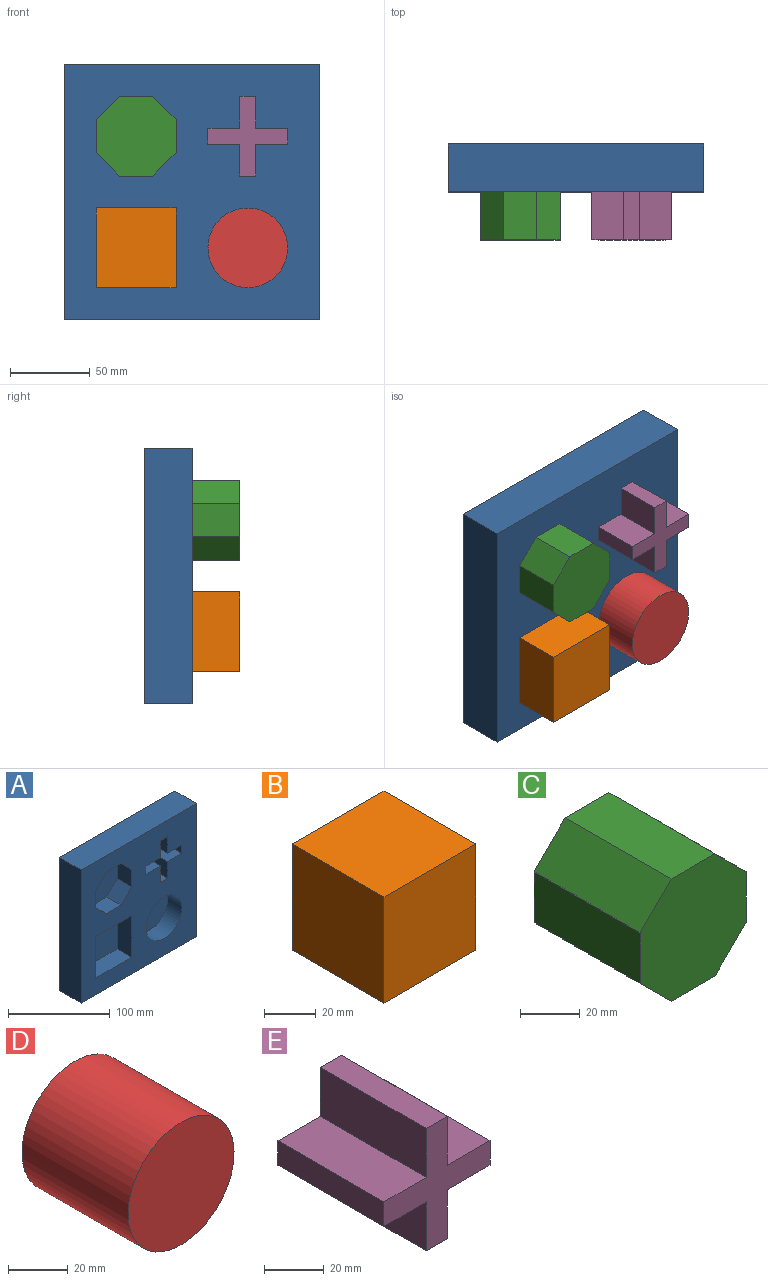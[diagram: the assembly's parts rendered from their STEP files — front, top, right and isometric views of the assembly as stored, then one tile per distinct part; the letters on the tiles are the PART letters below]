
ASSEMBLY  parts=5 mates=4
PART A: 35 faces, bbox 160x30x160 mm
  f0: plane 160x160mm, normal (0,-1,0), area 18165.4mm2, adj f1,f2,f3,f4,f6,f7,f8,f9
  f1: plane 160x30mm, normal (0,0,1), area 4800mm2, adj f0,f2,f4,f5
  f2: plane 160x30mm, normal (-1,0,0), area 4800mm2, adj f0,f1,f3,f5
  f3: plane 160x30mm, normal (0,0,-1), area 4800mm2, adj f0,f2,f4,f5
  f4: plane 160x30mm, normal (1,0,0), area 4800mm2, adj f0,f1,f3,f5
  f5: plane 160x160mm, normal (0,1,0), area 25600mm2, adj f1,f2,f3,f4
  f6: plane 20x14.64mm, normal (-0.71,0,-0.71), area 414.2mm2, adj f0,f7,f13,f14
  f7: plane 20.71x20mm, normal (0,0,-1), area 414.2mm2, adj f0,f6,f8,f14
  f8: plane 20x14.64mm, normal (0.71,0,-0.71), area 414.2mm2, adj f0,f7,f9,f14
  f9: plane 20.71x20mm, normal (1,0,0), area 414.2mm2, adj f0,f8,f10,f14
  f10: plane 20x14.64mm, normal (0.71,0,0.71), area 414.2mm2, adj f0,f9,f11,f14
  f11: plane 20.71x20mm, normal (0,0,1), area 414.2mm2, adj f0,f10,f12,f14
  f12: plane 20x14.64mm, normal (-0.71,0,0.71), area 414.2mm2, adj f0,f11,f13,f14
  f13: plane 20.71x20mm, normal (-1,0,0), area 414.2mm2, adj f0,f6,f12,f14
  f14: plane 50x50mm, normal (0,-1,0), area 2071.1mm2, adj f6,f7,f8,f9,f10,f11,f12,f13
  f15: cylinder r=25mm len=50mm, axis (0,-1,0), area 3141.6mm2, adj f0,f16
  f16: plane 50x50mm, normal (0,-1,0), area 1963.5mm2, adj f15
  f17: plane 50x20mm, normal (0,0,-1), area 1000mm2, adj f0,f18,f20,f21
  f18: plane 50x20mm, normal (1,0,0), area 1000mm2, adj f0,f17,f19,f21
  f19: plane 50x20mm, normal (0,0,1), area 1000mm2, adj f0,f18,f20,f21
  f20: plane 50x20mm, normal (-1,0,0), area 1000mm2, adj f0,f17,f19,f21
  f21: plane 50x50mm, normal (0,-1,0), area 2500mm2, adj f17,f18,f19,f20
  f22: plane 20x10mm, normal (0,0,-1), area 200mm2, adj f0,f23,f33,f34
  f23: plane 20x20mm, normal (1,0,0), area 400mm2, adj f0,f22,f24,f34
  f24: plane 20x20mm, normal (0,0,-1), area 400mm2, adj f0,f23,f25,f34
  f25: plane 20x10mm, normal (1,0,0), area 200mm2, adj f0,f24,f26,f34
  f26: plane 20x20mm, normal (0,0,1), area 400mm2, adj f0,f25,f27,f34
  f27: plane 20x20mm, normal (1,0,0), area 400mm2, adj f0,f26,f28,f34
  f28: plane 20x10mm, normal (0,0,1), area 200mm2, adj f0,f27,f29,f34
  f29: plane 20x20mm, normal (-1,0,0), area 400mm2, adj f0,f28,f30,f34
  f30: plane 20x20mm, normal (0,0,1), area 400mm2, adj f0,f29,f31,f34
  f31: plane 20x10mm, normal (-1,0,0), area 200mm2, adj f0,f30,f32,f34
  f32: plane 20x20mm, normal (0,0,-1), area 400mm2, adj f0,f31,f33,f34
  f33: plane 20x20mm, normal (-1,0,0), area 400mm2, adj f0,f22,f32,f34
  f34: plane 50x50mm, normal (0,-1,0), area 900mm2, adj f22,f23,f24,f25,f26,f27,f28,f29
PART B: 6 faces, bbox 50x50x50 mm
  f0: plane 50x50mm, normal (0,0,1), area 2500mm2, adj f1,f3,f4,f5
  f1: plane 50x50mm, normal (-1,0,0), area 2500mm2, adj f0,f2,f4,f5
  f2: plane 50x50mm, normal (0,0,-1), area 2500mm2, adj f1,f3,f4,f5
  f3: plane 50x50mm, normal (1,0,0), area 2500mm2, adj f0,f2,f4,f5
  f4: plane 50x50mm, normal (0,-1,0), area 2500mm2, adj f0,f1,f2,f3
  f5: plane 50x50mm, normal (0,1,0), area 2500mm2, adj f0,f1,f2,f3
PART C: 10 faces, bbox 50x50x50 mm
  f0: plane 50x14.64mm, normal (0.71,0,0.71), area 1035.5mm2, adj f1,f7,f8,f9
  f1: plane 50x20.71mm, normal (0,0,1), area 1035.5mm2, adj f0,f2,f8,f9
  f2: plane 50x14.64mm, normal (-0.71,0,0.71), area 1035.5mm2, adj f1,f3,f8,f9
  f3: plane 50x20.71mm, normal (-1,0,0), area 1035.5mm2, adj f2,f4,f8,f9
  f4: plane 50x14.64mm, normal (-0.71,0,-0.71), area 1035.5mm2, adj f3,f5,f8,f9
  f5: plane 50x20.71mm, normal (0,0,-1), area 1035.5mm2, adj f4,f6,f8,f9
  f6: plane 50x14.64mm, normal (0.71,0,-0.71), area 1035.5mm2, adj f5,f7,f8,f9
  f7: plane 50x20.71mm, normal (1,0,0), area 1035.5mm2, adj f0,f6,f8,f9
  f8: plane 50x50mm, normal (0,-1,0), area 2071.1mm2, adj f0,f1,f2,f3,f4,f5,f6,f7
  f9: plane 50x50mm, normal (0,1,0), area 2071.1mm2, adj f0,f1,f2,f3,f4,f5,f6,f7
PART D: 3 faces, bbox 50x50x50 mm
  f0: cylinder r=25mm len=50mm, axis (0,1,0), area 7854mm2, adj f1,f2
  f1: plane 50x50mm, normal (0,-1,0), area 1963.5mm2, adj f0
  f2: plane 50x50mm, normal (0,1,0), area 1963.5mm2, adj f0
PART E: 14 faces, bbox 50.1x50x50 mm
  f0: plane 50x10mm, normal (0,0,1), area 500mm2, adj f1,f11,f12,f13
  f1: plane 50x20mm, normal (-1,0,0), area 1000mm2, adj f0,f2,f12,f13
  f2: plane 50x20mm, normal (0,0,1), area 1000mm2, adj f1,f3,f12,f13
  f3: plane 50x10mm, normal (-1,0,0), area 500mm2, adj f2,f4,f12,f13
  f4: plane 50x20mm, normal (0,0,-1), area 1000mm2, adj f3,f5,f12,f13
  f5: plane 50x20mm, normal (-1,0,0), area 1000mm2, adj f4,f6,f12,f13
  f6: plane 50x10mm, normal (0,0,-1), area 500mm2, adj f5,f7,f12,f13
  f7: plane 50x20mm, normal (1,0,0), area 1000mm2, adj f6,f8,f12,f13
  f8: plane 50x20.1mm, normal (0,0,-1), area 1005mm2, adj f7,f9,f12,f13
  f9: plane 50x10mm, normal (1,0,0), area 500mm2, adj f8,f10,f12,f13
  f10: plane 50x20.1mm, normal (0,0,1), area 1005mm2, adj f9,f11,f12,f13
  f11: plane 50x20mm, normal (1,0,0), area 1000mm2, adj f0,f10,f12,f13
  f12: plane 50.1x50mm, normal (0,-1,0), area 901mm2, adj f0,f1,f2,f3,f4,f5,f6,f7
  f13: plane 50.1x50mm, normal (0,1,0), area 901mm2, adj f0,f1,f2,f3,f4,f5,f6,f7
PLACE A t=(-189.32,-103.87,8.96)mm
PLACE B t=(-183.6,-113.87,-65.67)mm
PLACE C t=(-183.33,-113.87,11.77)mm
PLACE D t=(-190.98,-113.87,13.15)mm
PLACE E t=(-189.09,-113.87,24.56)mm
MATE fastened A.f21 <-> B.f5  axis (0,-1,0) through (-224.32,-113.87,-26.04)mm
MATE fastened A.f15 <-> D.f0  axis (0,-1,0) through (-154.32,-113.87,-26.04)mm
MATE fastened A.f14 <-> C.f9  axis (0,-1,0) through (-224.32,-113.87,43.96)mm
MATE fastened A.f34 <-> E.f13  axis (0,-1,0) through (-154.32,-113.87,43.96)mm
